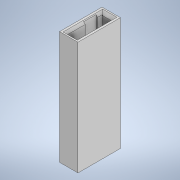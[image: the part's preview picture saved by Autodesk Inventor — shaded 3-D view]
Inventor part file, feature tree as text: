
AUTODESK INVENTOR PART (.ipt)
format: ipt  version: 2020 (Build 240168000, 168)  size: 143,872 bytes
history: native  units: mm
features: move_body x7, extrude x2, direct_edit x2, sketch x2, chamfer x1
ambient origin geometry x8: Origin, YZ Plane, XZ Plane, XY Plane, X Axis, Y Axis, Z Axis, Center Point
bodies: Solid1 (feature_tree)
feature tree (14):
  extrude  "Extrusion1"  Depth=12.0mm
  chamfer  "Chamfer1"  Distance=30.0mm
  direct_edit  "Direct Edit1"
  extrude  "Extrusion2"  Depth=1.0mm TaperAngle=45.0deg
  direct_edit  "Direct Edit2"
  sketch  "Sketch1"  dims[d0=3.0mm d1=12.0mm]
  sketch  "Sketch2"  dims[d2=2.0mm d3=30.0mm d4=0.0mm d5=1.0mm d6=2.0mm d7=45.0deg d8=0.0mm d9=0.0mm d10=-0.2mm d11=0.0mm d12=0.0mm d13=-0.2mm d14=0.0mm d15=0.0mm d16=-0.25mm d17=0.0mm d18=0.0mm d19=-0.5mm d20=0.0mm d21=0.0mm d22=-0.25mm d23=0.0mm d24=0.0mm d25=-0.5mm d26=2.25mm d27=2.25mm d28=4.5mm d29=0.0mm d30=0.0mm d31=0.0mm d32=0.0mm d33=10.0mm]
  move_body  "Move1"
  move_body  "Move2"
  move_body  "Move3"
  move_body  "Move4"
  move_body  "Move5"
  move_body  "Move6"
  move_body  "Move7"
